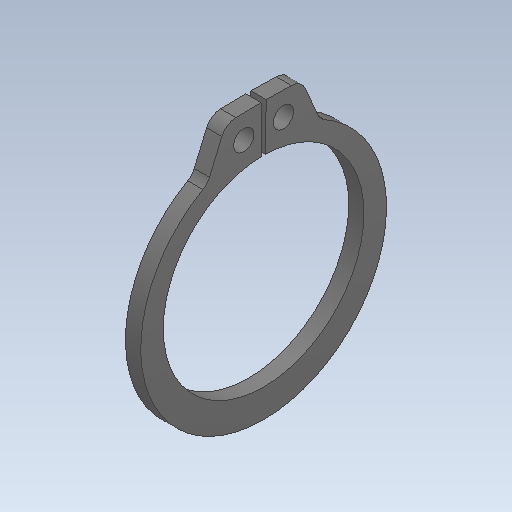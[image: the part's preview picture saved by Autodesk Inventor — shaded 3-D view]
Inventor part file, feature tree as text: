
AUTODESK INVENTOR PART (.ipt)
format: ipt  version: 2020 (Build 240168000, 168)  size: 111,104 bytes
history: native  units: in
note: dims shown in document units (in); Inventor stores cm internally (conversion verified against a paired STEP export)
features: fillet x1
ambient origin geometry x8: Origin, YZ Plane, XZ Plane, XY Plane, X Axis, Y Axis, Z Axis, Center Point
bodies: Solid1 (feature_tree)
feature tree (1):
  fillet  "Fillet1"  [1 undecoded]
note: 1 required parameter value undecoded (feature->parameter linkage not recoverable at this tier; creation-order binding heuristic only, values carry confidence <= 0.55)
